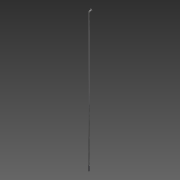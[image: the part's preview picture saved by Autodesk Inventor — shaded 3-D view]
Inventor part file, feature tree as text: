
AUTODESK INVENTOR PART (.ipt)
format: ipt  version: 2015 (Build 190159000, 159)  size: 113,152 bytes
history: native  units: mm
features: sketch x4, other x3, extrude x1, chamfer x1, thread x1
ambient origin geometry x8: Origin, YZ Plane, XZ Plane, XY Plane, X Axis, Y Axis, Z Axis, Center Point
bodies: Body1 (feature_tree)
feature tree (10):
  other  "Szprycha"
  other  "Bryła1"
  other  "Główka"
  extrude  "Połączenie z nyplem"  Depth=2.0mm
  chamfer  "Faza1"  Distance=266.0mm
  thread  "Gwint2"
  sketch  "Szkic1"
  sketch  "Szkic4"
  sketch  "Szkic5"
  sketch  "Szkic6"
